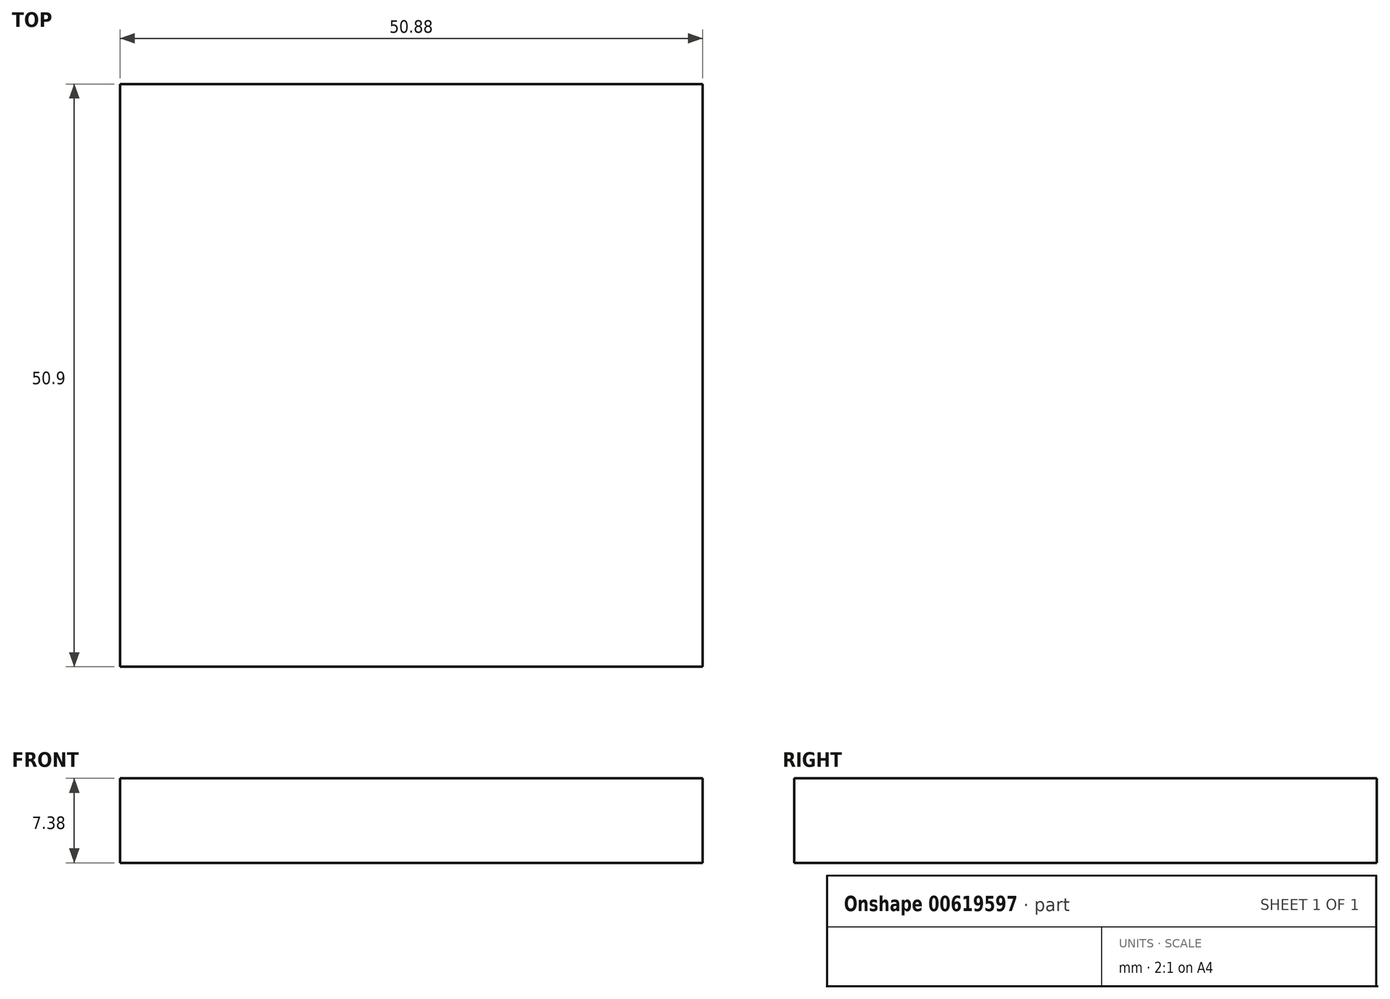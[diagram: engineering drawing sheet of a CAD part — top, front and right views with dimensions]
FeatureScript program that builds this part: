
annotation { "Feature Type Name" : "Feature", "Feature Type Description" : "" }
export const myFeature = defineFeature(function(context is Context, id is Id, definition is map)
    precondition{}
    {
        {
            var Q0;
            Q0=qCreatedBy(makeId("Top.planeOp"),FACE);
            var sketch = newSketch(context, id + "F0", { "sketchPlane" : qUnion([Q0])});
            skLineSegment(sketch, "E0.bottom", {"start": v(-25.44, 25.45) * mm, "end": v(25.44, 25.45) * mm});
            skLineSegment(sketch, "E0.top", {"start": v(-25.44, -25.45) * mm, "end": v(25.44, -25.45) * mm});
            skLineSegment(sketch, "E0.left", {"start": v(-25.44, 25.45) * mm, "end": v(-25.44, -25.45) * mm});
            skLineSegment(sketch, "E0.right", {"start": v(25.44, 25.45) * mm, "end": v(25.44, -25.45) * mm});
            skPoint(sketch, "E0.middle", {"position": v(0, 0) * mm});
            skSolve(sketch);
        }
        {
            var Q0;
            Q0 = qSketchRegion(id + "F0", true);
            extrude(context, id + "F1", {"entities" : qUnion([Q0]), "depth" : 7.38 * mm, "offsetDistance" : 25.4 * mm});
        }
    });
